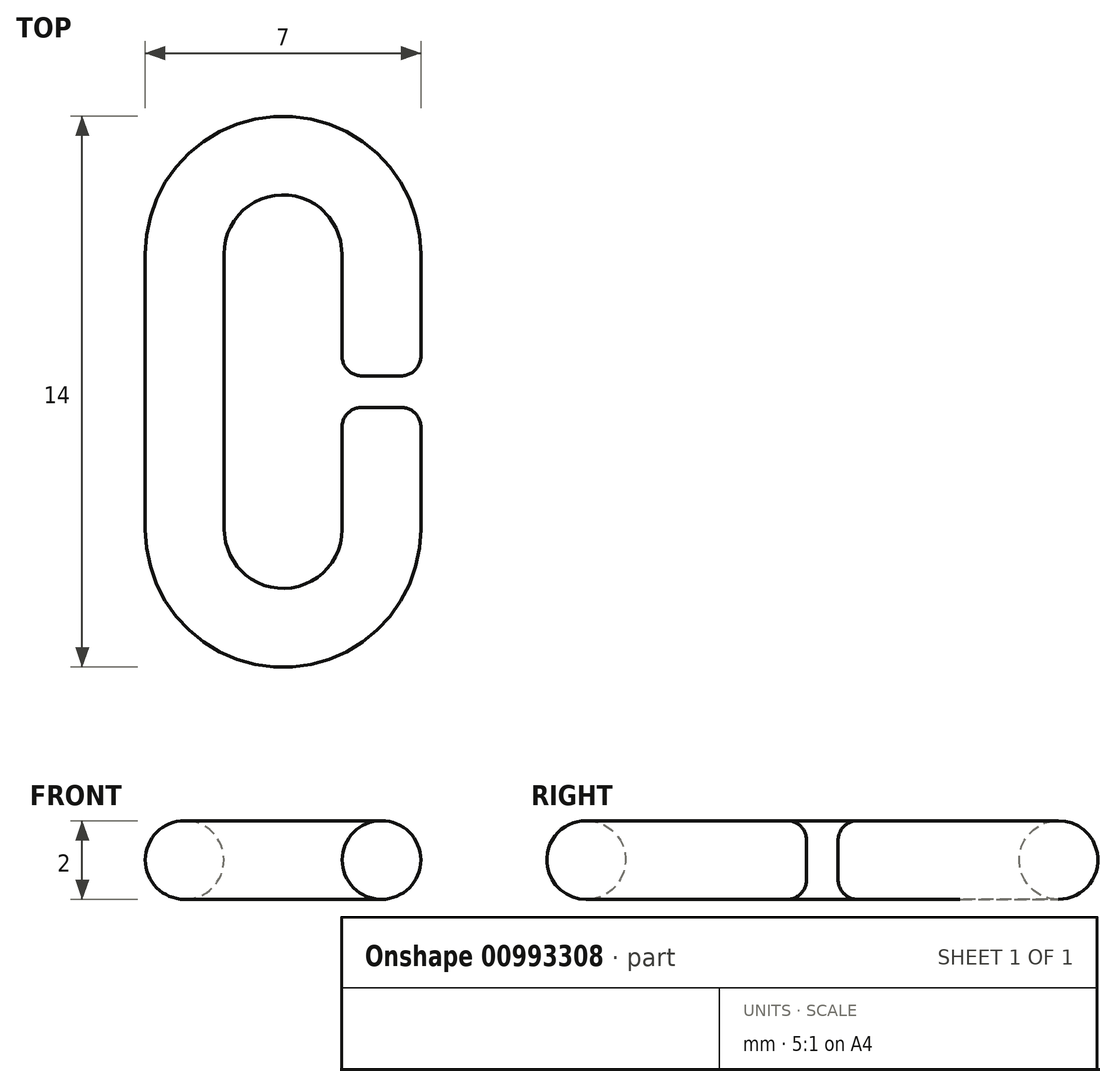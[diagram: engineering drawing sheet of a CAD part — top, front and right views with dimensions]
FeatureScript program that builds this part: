
annotation { "Feature Type Name" : "Feature", "Feature Type Description" : "" }
export const myFeature = defineFeature(function(context is Context, id is Id, definition is map)
    precondition{}
    {
        {
            var Q0;
            Q0=qCreatedBy(makeId("Top.planeOp"),FACE);
            var sketch = newSketch(context, id + "F0", { "sketchPlane" : qUnion([Q0])});
            skLineSegment(sketch, "E0", {"start": v(0, 6.08) * mm, "end": v(0, -5.2) * mm, "construction": true});
            skLineSegment(sketch, "E1", {"start": v(-6.48, 0) * mm, "end": v(5.79, 0) * mm, "construction": true});
            skArc(sketch, "E2", {"start": v(2.5, 3.5) * mm, "mid": v(0, 6) * mm, "end": v(-2.5, 3.5) * mm});
            skArc(sketch, "E3", {"start": v(-2.5, -3.5) * mm, "mid": v(0, -6) * mm, "end": v(2.5, -3.5) * mm});
            skLineSegment(sketch, "E4", {"start": v(-2.5, 3.5) * mm, "end": v(-2.5, -3.5) * mm});
            skLineSegment(sketch, "E5", {"start": v(2.5, 3.5) * mm, "end": v(2.5, -3.5) * mm});
            skSolve(sketch);
        }
        {
            var Q0;
            Q0=qCreatedBy(makeId("Front.planeOp"),FACE);
            var sketch = newSketch(context, id + "F1", { "sketchPlane" : qUnion([Q0])});
            skCircle(sketch, "E6", {"center": v(-2.5, 0) * mm, "radius": 1 * mm});
            skSolve(sketch);
        }
        {
            var Q0;
            Q0 = qSketchRegion(id + "F1", true);
            var Q1;
            Q1 = qConstructionFilter(qBodyType(qCreatedBy(id + "F0" ,EDGE), BodyType.WIRE), ConstructionObject.NO);
            sweep(context, id + "F2", {"profiles" : qUnion([Q0]), "path" : qUnion([Q1])});
        }
        {
            var Q0;
            Q0=qCreatedBy(makeId("Top.planeOp"),FACE);
            var sketch = newSketch(context, id + "F3", { "sketchPlane" : qUnion([Q0])});
            skLineSegment(sketch, "E7", {"start": v(6.69, 0) * mm, "end": v(0.8, 0) * mm, "construction": true});
            skLineSegment(sketch, "E8.bottom", {"start": v(10, 0.4) * mm, "end": v(0, 0.4) * mm});
            skLineSegment(sketch, "E8.top", {"start": v(10, -0.4) * mm, "end": v(0, -0.4) * mm});
            skLineSegment(sketch, "E8.left", {"start": v(10, 0.4) * mm, "end": v(10, -0.4) * mm});
            skLineSegment(sketch, "E8.right", {"start": v(0, 0.4) * mm, "end": v(0, -0.4) * mm});
            skSolve(sketch);
        }
        {
            var Q0;
            Q0=makeQuery(id+"F3.imprint","IMPRINT",FACE,{"disambiguationData":[TD([[makeQuery(id+"F3.imprint","IMPRINT",EDGE,{"derivedFrom":sQuery(id+"F3.wireOp",EDGE,"E8.bottom")}),1.0]])]});
            extrude(context, id + "F4", {"entities" : qUnion([Q0]), "operationType" : NewBodyOperationType.REMOVE, "endBound" : BoundingType.SYMMETRIC, "oppositeDirection" : true, "depth" : 25 * mm, "offsetDistance" : 25 * mm});
        }
        {
            var Q0;
            Q0=makeQuery(id+"F4.boolean.opBoolean","INTERSECT",EDGE,{"derivedFrom":[makeQuery(id+"F2.opSweep","SWEPT_FACE",FACE,{"disambiguationData":[OSD([sQuery(id+"F0.wireOp",EDGE,"E5"),sQuery(id+"F1.wireOp",EDGE,"E6")])]}),makeQuery(id+"F4.opExtrude","SWEPT_FACE",FACE,{"disambiguationData":[OSD([sQuery(id+"F3.wireOp",EDGE,"E8.bottom")])]})]});
            var Q1;
            Q1=makeQuery(id+"F4.boolean.opBoolean","INTERSECT",EDGE,{"derivedFrom":[makeQuery(id+"F2.opSweep","SWEPT_FACE",FACE,{"disambiguationData":[OSD([sQuery(id+"F0.wireOp",EDGE,"E5"),sQuery(id+"F1.wireOp",EDGE,"E6")])]}),makeQuery(id+"F4.opExtrude","SWEPT_FACE",FACE,{"disambiguationData":[OSD([sQuery(id+"F3.wireOp",EDGE,"E8.top")])]})]});
            fillet(context, id + "F5", {"entities" : qUnion([Q0, Q1]), "radius" : .5 * mm, "tangentPropagation" : true, "allowEdgeOverflow" : false});
        }
    });
